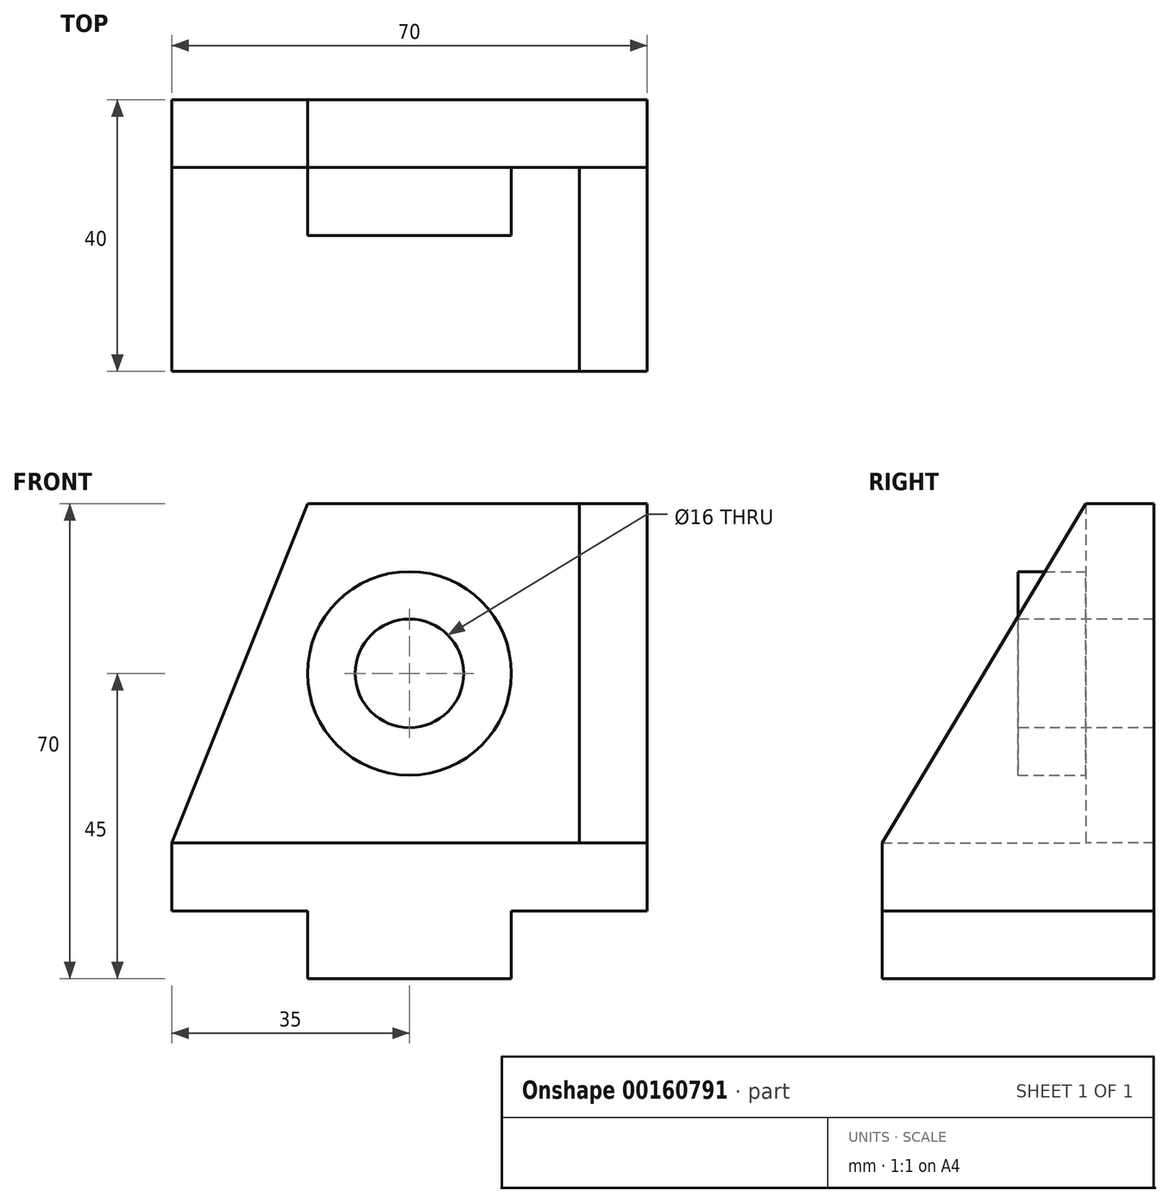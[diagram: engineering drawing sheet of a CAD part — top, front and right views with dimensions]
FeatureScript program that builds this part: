
annotation { "Feature Type Name" : "Feature", "Feature Type Description" : "" }
export const myFeature = defineFeature(function(context is Context, id is Id, definition is map)
    precondition{}
    {
        {
            var Q0;
            Q0=qCreatedBy(makeId("Front.planeOp"),FACE);
            var sketch = newSketch(context, id + "F0", { "sketchPlane" : qUnion([Q0])});
            skLineSegment(sketch, "E0", {"start": v(-35, 0) * mm, "end": v(35, 0) * mm});
            skLineSegment(sketch, "E1", {"start": v(35, 0) * mm, "end": v(35, -10) * mm});
            skLineSegment(sketch, "E2", {"start": v(35, -10) * mm, "end": v(15, -10) * mm});
            skLineSegment(sketch, "E3", {"start": v(15, -10) * mm, "end": v(15, -20) * mm});
            skLineSegment(sketch, "E4", {"start": v(15, -20) * mm, "end": v(-15, -20) * mm});
            skLineSegment(sketch, "E5", {"start": v(-15, -20) * mm, "end": v(-15, -10) * mm});
            skLineSegment(sketch, "E6", {"start": v(-15, -10) * mm, "end": v(-35, -10) * mm});
            skLineSegment(sketch, "E7", {"start": v(-35, -10) * mm, "end": v(-35, 0) * mm});
            skSolve(sketch);
        }
        {
            var Q0;
            Q0=makeQuery(id+"F0.imprint","IMPRINT",FACE,{"disambiguationData":[TD([[makeQuery(id+"F0.imprint","IMPRINT",EDGE,{"derivedFrom":sQuery(id+"F0.wireOp",EDGE,"E0")}),-1.0]])]});
            extrude(context, id + "F1", {"entities" : qUnion([Q0]), "depth" : 40 * mm});
        }
        {
            var Q0;
            Q0=makeQuery(id+"F1.opExtrude","SWEPT_FACE",FACE,{"disambiguationData":[OSD([sQuery(id+"F0.wireOp",EDGE,"E0")])]});
            var sketch = newSketch(context, id + "F2", { "sketchPlane" : qUnion([Q0])});
            skLineSegment(sketch, "E8", {"start": v(-35, 0) * mm, "end": v(35, 0) * mm});
            skLineSegment(sketch, "E9", {"start": v(35, 0) * mm, "end": v(35, -40) * mm});
            skLineSegment(sketch, "E10", {"start": v(35, -40) * mm, "end": v(25, -40) * mm});
            skLineSegment(sketch, "E11", {"start": v(25, -40) * mm, "end": v(25, -10) * mm});
            skLineSegment(sketch, "E12", {"start": v(25, -10) * mm, "end": v(-35, -10) * mm});
            skLineSegment(sketch, "E13", {"start": v(-35, -10) * mm, "end": v(-35, 0) * mm});
            skSolve(sketch);
        }
        {
            var Q0;
            Q0=makeQuery(id+"F2.imprint","IMPRINT",FACE,{"disambiguationData":[TD([[makeQuery(id+"F2.imprint","IMPRINT",EDGE,{"derivedFrom":sQuery(id+"F2.wireOp",EDGE,"E8")}),-1.0]])]});
            extrude(context, id + "F3", {"entities" : qUnion([Q0]), "operationType" : NewBodyOperationType.ADD, "depth" : 50 * mm});
        }
        {
            var Q0;
            Q0=makeQuery(id+"F3.opExtrude","SWEPT_FACE",FACE,{"disambiguationData":[OSD([sQuery(id+"F2.wireOp",EDGE,"E12")])]});
            var sketch = newSketch(context, id + "F4", { "sketchPlane" : qUnion([Q0])});
            skLineSegment(sketch, "E14", {"start": v(-35, 50) * mm, "end": v(-15, 50) * mm});
            skLineSegment(sketch, "E15", {"start": v(-15, 50) * mm, "end": v(-35, 0) * mm});
            skLineSegment(sketch, "E16", {"start": v(-35, 0) * mm, "end": v(-35, 50) * mm});
            skSolve(sketch);
        }
        {
            var Q0;
            Q0=makeQuery(id+"F4.imprint","IMPRINT",FACE,{"disambiguationData":[TD([[makeQuery(id+"F4.imprint","IMPRINT",EDGE,{"derivedFrom":sQuery(id+"F4.wireOp",EDGE,"E14")}),1.0]])]});
            extrude(context, id + "F5", {"entities" : qUnion([Q0]), "operationType" : NewBodyOperationType.REMOVE, "endBound" : BoundingType.UP_TO_NEXT, "oppositeDirection" : true, "depth" : 25 * mm});
        }
        {
            var Q0;
            Q0=makeQuery(id+"F3.opExtrude","SWEPT_FACE",FACE,{"disambiguationData":[OSD([sQuery(id+"F2.wireOp",EDGE,"E11")])]});
            var sketch = newSketch(context, id + "F6", { "sketchPlane" : qUnion([Q0])});
            skLineSegment(sketch, "E17", {"start": v(10, 50) * mm, "end": v(40, 50) * mm});
            skLineSegment(sketch, "E18", {"start": v(40, 50) * mm, "end": v(40, 0) * mm});
            skLineSegment(sketch, "E19", {"start": v(40, 0) * mm, "end": v(10, 50) * mm});
            skSolve(sketch);
        }
        {
            var Q0;
            Q0=makeQuery(id+"F6.imprint","IMPRINT",FACE,{"disambiguationData":[TD([[makeQuery(id+"F6.imprint","IMPRINT",EDGE,{"derivedFrom":sQuery(id+"F6.wireOp",EDGE,"E17")}),1.0]])]});
            extrude(context, id + "F7", {"entities" : qUnion([Q0]), "operationType" : NewBodyOperationType.REMOVE, "endBound" : BoundingType.UP_TO_NEXT, "oppositeDirection" : true, "depth" : 25 * mm});
        }
        {
            var Q0;
            Q0=makeQuery(id+"F3.opExtrude","SWEPT_FACE",FACE,{"disambiguationData":[OSD([sQuery(id+"F2.wireOp",EDGE,"E12")])]});
            var sketch = newSketch(context, id + "F8", { "sketchPlane" : qUnion([Q0])});
            skCircle(sketch, "E20", {"center": v(0, 25) * mm, "radius": 15 * mm});
            skSolve(sketch);
        }
        {
            var Q0;
            Q0=makeQuery(id+"F8.imprint","IMPRINT",FACE,{"disambiguationData":[TD([[makeQuery(id+"F8.imprint","IMPRINT",EDGE,{"derivedFrom":sQuery(id+"F8.wireOp",EDGE,"E20")}),1.0]])]});
            extrude(context, id + "F9", {"entities" : qUnion([Q0]), "operationType" : NewBodyOperationType.ADD, "depth" : 10 * mm});
        }
        {
            var Q0;
            Q0=makeQuery(id+"F9.opExtrude","CAP_FACE",FACE,{"disambiguationData":[OSD([sQuery(id+"F8.wireOp",EDGE,"E20")])],"isStart":false});
            var sketch = newSketch(context, id + "F10", { "sketchPlane" : qUnion([Q0])});
            skPoint(sketch, "E21", {"position": v(0, 25) * mm});
            skSolve(sketch);
        }
        {
            var Q0;
            Q0=sQuery(id+"F10.wireOp",VERTEX,"E21");
            var Q1;
            Q1=makeQuery(id+"F1.opExtrude","SWEPT_BODY",BODY,{"disambiguationData":[OSD([sQuery(id+"F0.wireOp",EDGE,"E0"),sQuery(id+"F0.wireOp",EDGE,"E1"),sQuery(id+"F0.wireOp",EDGE,"E2"),sQuery(id+"F0.wireOp",EDGE,"E3"),sQuery(id+"F0.wireOp",EDGE,"E4"),sQuery(id+"F0.wireOp",EDGE,"E5"),sQuery(id+"F0.wireOp",EDGE,"E6"),sQuery(id+"F0.wireOp",EDGE,"E7")])]});
            hole(context, id + "F11", {"style" : HoleStyle.SIMPLE, "endStyle" : HoleEndStyle.THROUGH, "holeDiameter" : 16 * mm, "locations" : qUnion([Q0]), "scope" : qUnion([Q1]), "isTappedThrough" : true});
        }
    });
